# Revit family: Hager-Orion-IP65-D200-Cl.I-Steel_encl-630A-IT-it
name_source: partatom
category: Equipement électrique
units: mm (PartAtom-declared; Revit-internal decimal feet)

## family parameters
Configuration du panneau = Deux colonnes, circuits au sein
Cote de connecteur circulaire = Utiliser le diamètre
Couper avec des vides une fois chargée = Non
Hôte = Face
Partagée = Non
Point de calcul de pièce = Non
Type d'élément = Tableau de raccordement

## types (6) — shared parameters
Commentaires du type = Orion
EF000003 - Tipo di montaggio = EV000384 - A parete
EF000007 - colore = EV000270 - grigio
EF000116 - numero RAL = 7035
EF000118 - con piastra di montaggio = Oui
EF000339 - tipo di copertura = EV004216 - porta
EF000437 - numero di ingressi per conduttori = 2
EF001596 - Attacco Lampada = EV000179 - acciaio
EF003532 - adatto per uso esterno = Non
EF004293 - resistenza agli urti = EV008784 - IK10
EF004464 - tipo di porta = EV002646 - singolo
EF005474 - grado di protezione (IP) = EV006421 - IP65
EF006244 - coperchio/porta trasparente = Non
EF006306 - con serratura = Oui
EF007800 - adatto per parafulmine = Non
EF008873 - corrente nominale (In) = 630 A
EF009171 - spessore materiale porta/coperchio = 2 mm  [stored 0.00656168 ft]
EF009554 - numero delle aperture per la piastra della flangia = 2
EF015940 - Coprire con rilascio di sovrapressione = Non
Fabricant = Hager
HG000002 - Con porta = Oui
HG000003 - Gamma = Orion
HG000006 - Ad incasso = Non
HG000009 - Porta doppia a battente = Non
HG000010 - Porte asimmetriche = Non
HG000023 - Custodia a doppia sezione = Non
HG000024 - Altezza della sezione inferiore = 800 mm  [stored 2.62467 ft]
HG000026 - A pavimento = Non
zero-valued in all types: EF000218 - profondità di incasso, EF002950 - Numero moduli DIN, EF004427 - numero di moduli, Elévation par défaut, HG000027 - Altezza dello zoccolo

## per-type parameters (varying)
| type | EF000008 - Larghezza | EF000040 - Altezza | EF000049 - profondità | EF000266 - numero di file | EF001088 - possibilità di applicazione | EF001131 - profondità interna | EF001613 - Integrità del circuito | EF009170 - spessore materiale scatola | EF009212 - esecuzione coperchio | HG000004 - Codice produttore |
| A parete IP65 L300 A400 P200  - FL706L | 300 mm | 400 mm  [stored 1.31234 ft] | 200 mm  [stored 0.656168 ft] | 0 | Oui | 160 mm  [stored 0.524934 ft] | EV000494 - senza | 1 mm  [stored 0.00328084 ft] | EV000116 - chiuso | FL706L |
| A parete IP65 L300 A400 P200  - FL707L | 300 mm | 400 mm  [stored 1.31234 ft] | 200 mm  [stored 0.656168 ft] | 0 | Oui | 300 mm | EV000494 - senza | 1 mm  [stored 0.00328084 ft] | EV000116 - chiuso | FL707L |
| A parete IP65 L400 A400 P200  - FL708L | 400 mm  [stored 1.31234 ft] | 400 mm  [stored 1.31234 ft] | 200 mm  [stored 0.656168 ft] | 0 | Non | 200 mm  [stored 0.656168 ft] |  | 2 mm  [stored 0.00656168 ft] | EV009916 - con taglio | FL708L |
| A parete IP65 L400 A500 P200  - FL713L | 400 mm  [stored 1.31234 ft] | 500 mm  [stored 1.64042 ft] | 200 mm  [stored 0.656168 ft] | 1 | Oui | 200 mm  [stored 0.656168 ft] | EV000494 - senza | 1 mm  [stored 0.00328084 ft] | EV000116 - chiuso | FL713L |
| A parete IP65 L500 A500 P200  - FL712L | 500 mm  [stored 1.64042 ft] | 500 mm  [stored 1.64042 ft] | 200 mm  [stored 0.656168 ft] | 0 | Non | 200 mm  [stored 0.656168 ft] |  | 2 mm  [stored 0.00656168 ft] | EV009916 - con taglio | FL712L |
| A parete IP65 L800 A950 P300  - FL728L | 800 mm  [stored 2.62467 ft] | 950 mm  [stored 3.1168 ft] | 300 mm | 0 | Non | 300 mm |  | 2 mm  [stored 0.00656168 ft] | EV009916 - con taglio | FL728L |

note: [stored X ft] marks values corroborated as IEEE doubles in the binary element streams (Revit-internal decimal feet)

## geometry (parser evidence)
native form markers: Sweep x7
no freeform markers — native parametric forms only
